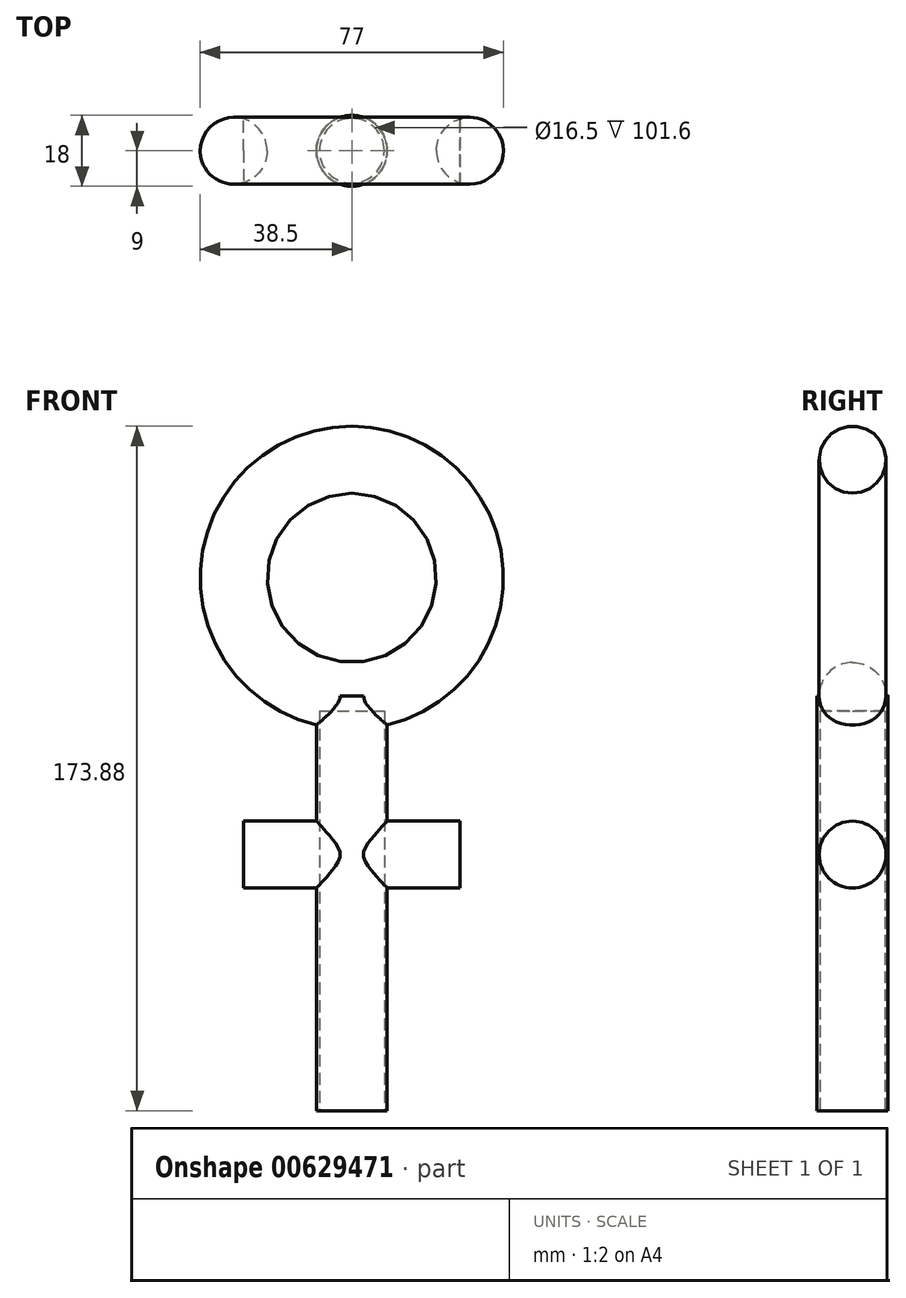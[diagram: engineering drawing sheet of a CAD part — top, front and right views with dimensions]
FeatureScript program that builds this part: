
annotation { "Feature Type Name" : "Feature", "Feature Type Description" : "" }
export const myFeature = defineFeature(function(context is Context, id is Id, definition is map)
    precondition{}
    {
        {
            var Q0;
            Q0=qCreatedBy(makeId("Front.planeOp"),FACE);
            var sketch = newSketch(context, id + "F0", { "sketchPlane" : qUnion([Q0])});
            skCircle(sketch, "E0", {"center": v(0, 0) * mm, "radius": 30 * mm});
            skLineSegment(sketch, "E1", {"start": v(0, -30) * mm, "end": v(0, -135.38) * mm});
            skLineSegment(sketch, "E2", {"start": v(0, -70.3) * mm, "end": v(-27.5, -70.3) * mm});
            skLineSegment(sketch, "E3.MirrorCS", {"start": v(0, -70.3) * mm, "end": v(27.5, -70.3) * mm});
            skPoint(sketch, "E4", {"position": v(-29.36, -6.17) * mm});
            skSolve(sketch);
        }
        {
            var Q0;
            Q0=sQuery(id+"F0.wireOp",EDGE,"E1");
            var Q1;
            Q1=sQuery(id+"F0.wireOp",VERTEX,"E1.end");
            cPlane(context, id + "F1", {"entities" : qUnion([Q0, Q1]), "cplaneType" : CPlaneType.CURVE_POINT, "offset" : 25.4 * mm, "width" : 152.4 * mm, "height" : 152.4 * mm});
        }
        {
            var Q0;
            Q0=qCreatedBy(id+"F1.planeOp",FACE);
            var sketch = newSketch(context, id + "F2", { "sketchPlane" : qUnion([Q0])});
            skCircle(sketch, "E5", {"center": v(0, 0) * mm, "radius": 9 * mm});
            skSolve(sketch);
        }
        {
            var Q0;
            Q0=makeQuery(id+"F2.imprint","IMPRINT",FACE,{"disambiguationData":[TD([[makeQuery(id+"F2.imprint","IMPRINT",EDGE,{"derivedFrom":sQuery(id+"F2.wireOp",EDGE,"E5")}),1.0]])]});
            var Q1;
            Q1=sQuery(id+"F0.wireOp",EDGE,"E1");
            sweep(context, id + "F3", {"profiles" : qUnion([Q0]), "path" : qUnion([Q1])});
        }
        {
            var Q0;
            Q0=sQuery(id+"F0.wireOp",EDGE,"E3.MirrorCS");
            var Q1;
            Q1=sQuery(id+"F0.wireOp",VERTEX,"E3.MirrorCS.end");
            cPlane(context, id + "F4", {"entities" : qUnion([Q0, Q1]), "cplaneType" : CPlaneType.CURVE_POINT, "offset" : 25.4 * mm, "width" : 152.4 * mm, "height" : 152.4 * mm});
        }
        {
            var Q0;
            Q0=qCreatedBy(id+"F4.planeOp",FACE);
            var sketch = newSketch(context, id + "F5", { "sketchPlane" : qUnion([Q0])});
            skCircle(sketch, "E6", {"center": v(0, -70.3) * mm, "radius": 8.5 * mm});
            skSolve(sketch);
        }
        {
            var Q0;
            Q0=makeQuery(id+"F5.imprint","IMPRINT",FACE,{"disambiguationData":[TD([[makeQuery(id+"F5.imprint","IMPRINT",EDGE,{"derivedFrom":sQuery(id+"F5.wireOp",EDGE,"E6")}),1.0]])]});
            var Q1;
            Q1=sQuery(id+"F0.wireOp",EDGE,"E2");
            var Q2;
            Q2=sQuery(id+"F0.wireOp",EDGE,"E3.MirrorCS");
            sweep(context, id + "F6", {"operationType" : NewBodyOperationType.ADD, "profiles" : qUnion([Q0]), "path" : qUnion([Q1, Q2])});
        }
        {
            var Q0;
            Q0=sQuery(id+"F0.wireOp",EDGE,"E0");
            var Q1;
            Q1=sQuery(id+"F0.wireOp",VERTEX,"E4");
            cPlane(context, id + "F7", {"entities" : qUnion([Q0, Q1]), "cplaneType" : CPlaneType.CURVE_POINT, "offset" : 25.4 * mm, "width" : 152.4 * mm, "height" : 152.4 * mm});
        }
        {
            var Q0;
            Q0=qCreatedBy(id+"F7.planeOp",FACE);
            var sketch = newSketch(context, id + "F8", { "sketchPlane" : qUnion([Q0])});
            skCircle(sketch, "E7", {"center": v(-30, 0) * mm, "radius": 8.5 * mm});
            skSolve(sketch);
        }
        {
            var Q0;
            Q0=makeQuery(id+"F8.imprint","IMPRINT",FACE,{"disambiguationData":[TD([[makeQuery(id+"F8.imprint","IMPRINT",EDGE,{"derivedFrom":sQuery(id+"F8.wireOp",EDGE,"E7")}),1.0]])]});
            var Q1;
            Q1=sQuery(id+"F0.wireOp",EDGE,"E0");
            sweep(context, id + "F9", {"operationType" : NewBodyOperationType.ADD, "profiles" : qUnion([Q0]), "path" : qUnion([Q1])});
        }
        {
            var Q0;
            Q0=makeQuery(id+"F3.opSweep","CAP_FACE",FACE,{"disambiguationData":[OSD([sQuery(id+"F0.wireOp",VERTEX,"E1.end"),sQuery(id+"F2.wireOp",EDGE,"E5")])],"isStart":true});
            var sketch = newSketch(context, id + "F10", { "sketchPlane" : qUnion([Q0])});
            skCircle(sketch, "E8", {"center": v(0, 0) * mm, "radius": 8.25 * mm});
            skSolve(sketch);
        }
        {
            var Q0;
            Q0=makeQuery(id+"F10.imprint","IMPRINT",FACE,{"disambiguationData":[TD([[makeQuery(id+"F10.imprint","IMPRINT",EDGE,{"derivedFrom":sQuery(id+"F10.wireOp",EDGE,"E8")}),1.0]])]});
            extrude(context, id + "F11", {"entities" : qUnion([Q0]), "operationType" : NewBodyOperationType.REMOVE, "oppositeDirection" : true, "depth" : 101.6 * mm, "offsetDistance" : 25.4 * mm});
        }
    });
